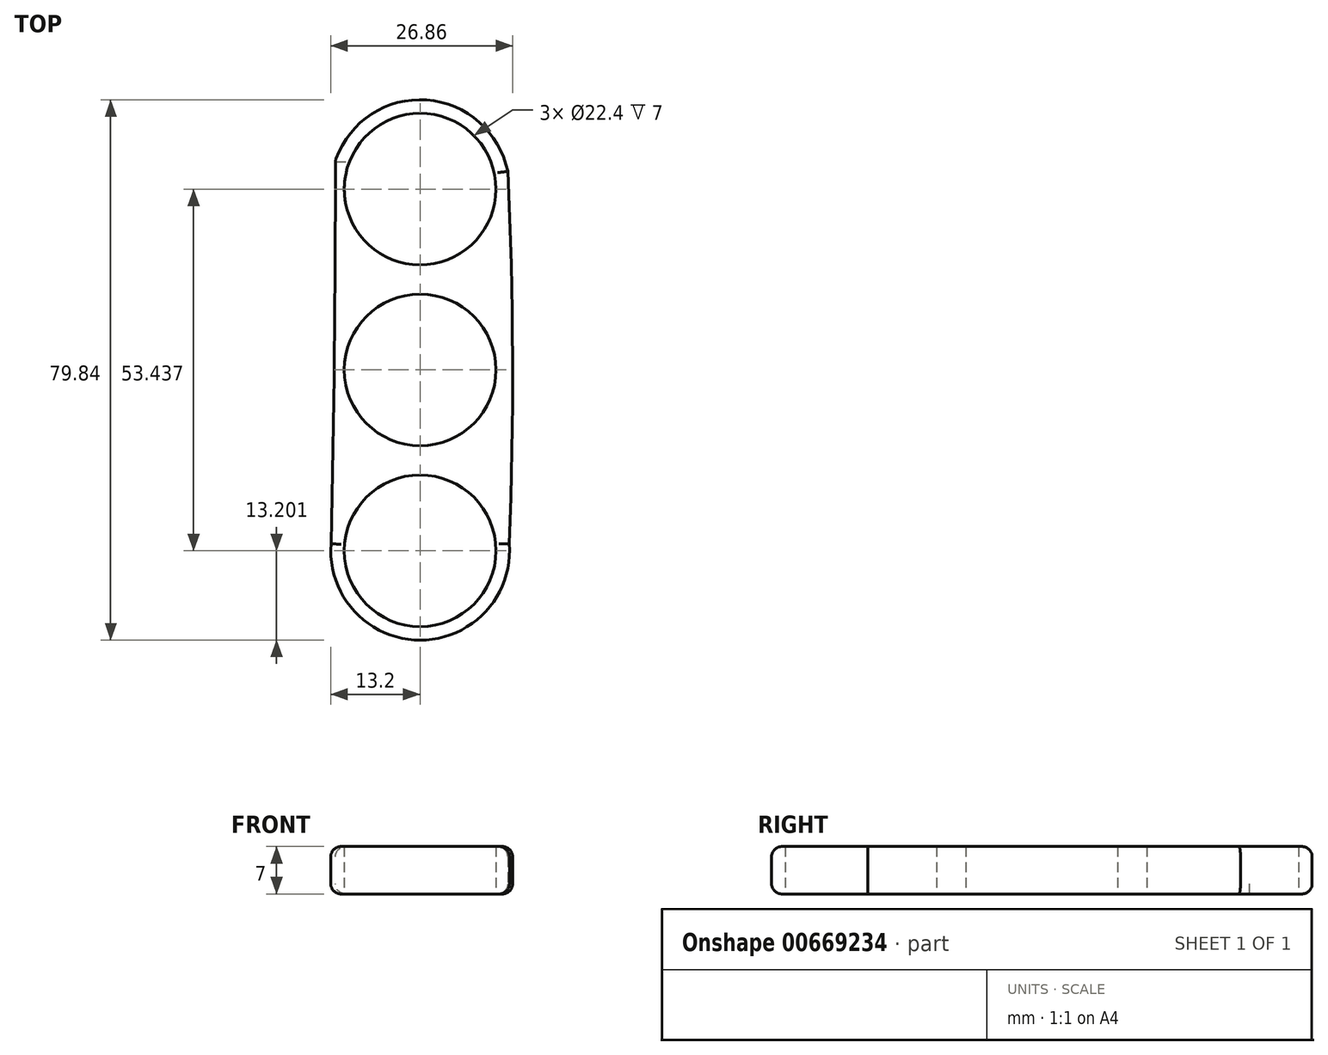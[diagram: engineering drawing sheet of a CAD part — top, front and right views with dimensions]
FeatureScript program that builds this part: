
annotation { "Feature Type Name" : "Feature", "Feature Type Description" : "" }
export const myFeature = defineFeature(function(context is Context, id is Id, definition is map)
    precondition{}
    {
        {
            var Q0;
            Q0=qCreatedBy(makeId("Top.planeOp"),FACE);
            var sketch = newSketch(context, id + "F0", { "sketchPlane" : qUnion([Q0])});
            skCircle(sketch, "E0", {"center": v(0, 0) * mm, "radius": 11.2 * mm});
            skCircle(sketch, "E1", {"center": v(0, 0) * mm, "radius": 13.2 * mm});
            skCircle(sketch, "E2", {"center": v(0, 26.72) * mm, "radius": 11.2 * mm});
            skCircle(sketch, "E3", {"center": v(0, 26.72) * mm, "radius": 13.2 * mm});
            skCircle(sketch, "E4.1.0", {"center": v(0, -26.72) * mm, "radius": 11.2 * mm});
            skCircle(sketch, "E4.1.1", {"center": v(0, -26.72) * mm, "radius": 13.2 * mm});
            skArc(sketch, "E5", {"start": v(13.16, -25.68) * mm, "mid": v(13.65, 1.83) * mm, "end": v(12.94, 29.33) * mm});
            skArc(sketch, "E6", {"start": v(-13.16, -25.68) * mm, "mid": v(-12.68, 2.63) * mm, "end": v(-12.5, 30.95) * mm});
            skSolve(sketch);
        }
        {
            var Q0;
            Q0=makeQuery(id+"F0.imprint","IMPRINT",FACE,{"disambiguationData":[TD([[makeQuery(id+"F0.imprint","IMPRINT",EDGE,{"derivedFrom":sQuery(id+"F0.wireOp",EDGE,"E2")}),-1.0]])]});
            var Q1;
            Q1=makeQuery(id+"F0.imprint","IMPRINT",FACE,{"disambiguationData":[TD([[makeQuery(id+"F0.imprint","IMPRINT",EDGE,{"derivedFrom":sQuery(id+"F0.wireOp",EDGE,"E0")}),-1.0]])]});
            var Q2;
            Q2=makeQuery(id+"F0.imprint","IMPRINT",FACE,{"disambiguationData":[TD([[makeQuery(id+"F0.imprint","IMPRINT",EDGE,{"derivedFrom":sQuery(id+"F0.wireOp",EDGE,"E4.1.0")}),-1.0]])]});
            var Q3;
            {var subQ3=sQuery(id+"F0.wireOp",EDGE,"E6");var subQ8=sQuery(id+"F0.wireOp",EDGE,"E1");var subQ9=makeQuery(id+"F0.imprint","INTERSECT",VERTEX,{"disambiguationData":[OD(0.0)],"derivedFrom":[subQ8,subQ3]});Q3=makeQuery(id+"F0.imprint","IMPRINT",FACE,{"disambiguationData":[TD([[makeQuery(id+"F0.imprint","IMPRINT",EDGE,{"disambiguationData":[TD([[subQ9,-1.0]])],"derivedFrom":subQ8}),-1.0]])]});}
            extrude(context, id + "F1", {"entities" : qUnion([Q0, Q1, Q2, Q3]), "depth" : 7 * mm, "offsetDistance" : 25 * mm});
        }
        {
            var Q0;
            Q0=makeQuery(id+"F1.opExtrude","CAP_EDGE",EDGE,{"disambiguationData":[OSD([sQuery(id+"F0.wireOp",EDGE,"E6")])],"isStart":false});
            var Q1;
            Q1=makeQuery(id+"F1.opExtrude","CAP_EDGE",EDGE,{"disambiguationData":[OSD([sQuery(id+"F0.wireOp",EDGE,"E3")])],"isStart":false});
            var Q2;
            Q2=makeQuery(id+"F1.opExtrude","CAP_EDGE",EDGE,{"disambiguationData":[OSD([sQuery(id+"F0.wireOp",EDGE,"E5")])],"isStart":false});
            var Q3;
            Q3=makeQuery(id+"F1.opExtrude","CAP_EDGE",EDGE,{"disambiguationData":[OSD([sQuery(id+"F0.wireOp",EDGE,"E4.1.1")])],"isStart":false});
            var Q4;
            Q4=makeQuery(id+"F1.opExtrude","CAP_EDGE",EDGE,{"disambiguationData":[OSD([sQuery(id+"F0.wireOp",EDGE,"E6")])],"isStart":true});
            fillet(context, id + "F2", {"entities" : qUnion([Q0, Q1, Q2, Q3, Q4]), "radius" : 1.5 * mm, "tangentPropagation" : true, "allowEdgeOverflow" : false});
        }
        {
            var Q0;
            Q0=makeQuery(id+"F1.opExtrude","CAP_EDGE",EDGE,{"disambiguationData":[OSD([sQuery(id+"F0.wireOp",EDGE,"E5")])],"isStart":true});
            var Q1;
            Q1=makeQuery(id+"F1.opExtrude","CAP_EDGE",EDGE,{"disambiguationData":[OSD([sQuery(id+"F0.wireOp",EDGE,"E4.1.1")])],"isStart":true});
            var Q2;
            Q2=makeQuery(id+"F1.opExtrude","CAP_EDGE",EDGE,{"disambiguationData":[OSD([sQuery(id+"F0.wireOp",EDGE,"E3")])],"isStart":true});
            fillet(context, id + "F3", {"entities" : qUnion([Q0, Q1, Q2]), "radius" : 1.5 * mm, "tangentPropagation" : true, "allowEdgeOverflow" : false});
        }
    });
